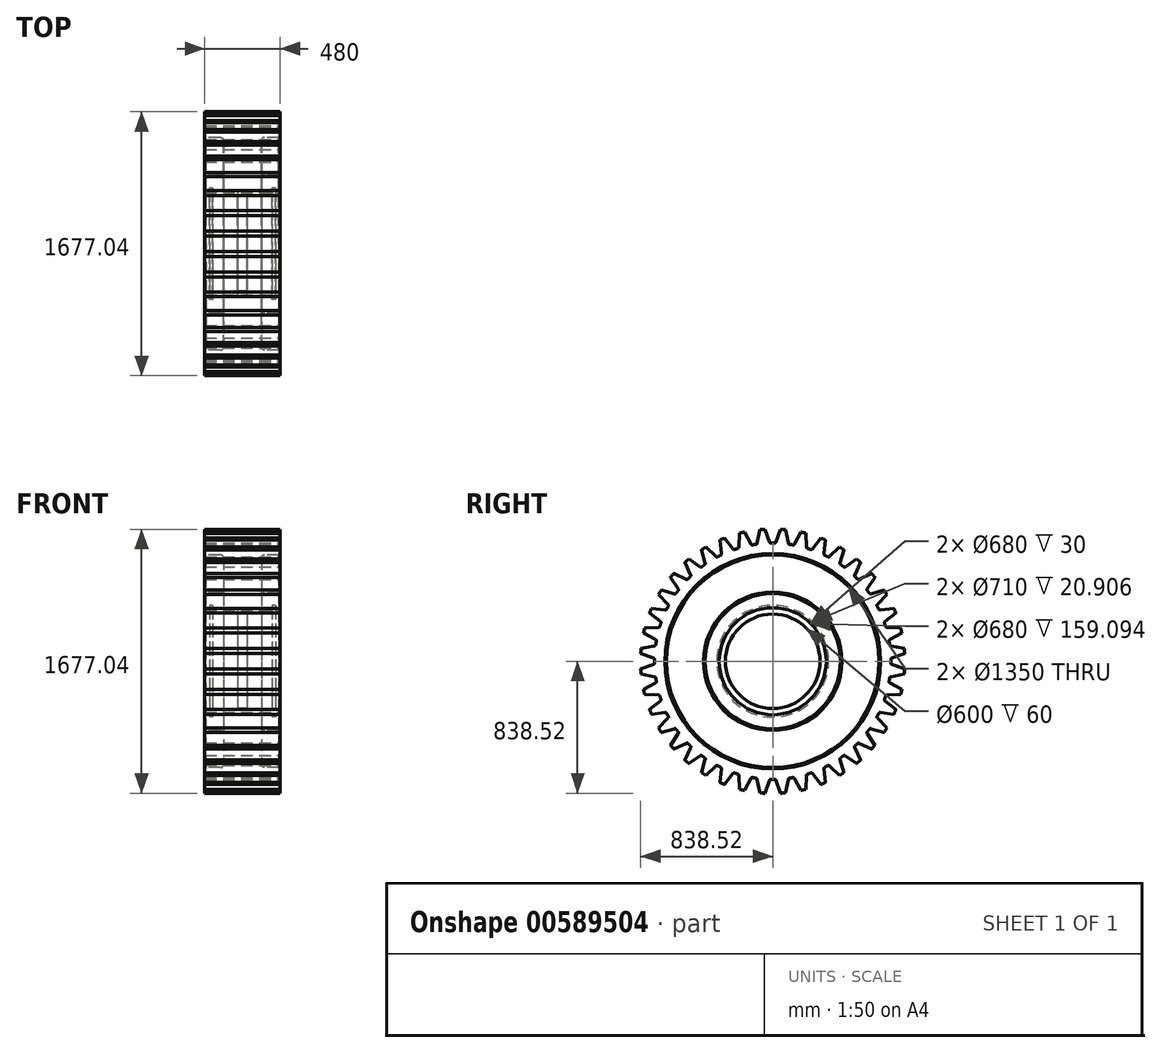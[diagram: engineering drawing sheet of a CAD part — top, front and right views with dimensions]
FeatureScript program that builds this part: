
annotation { "Feature Type Name" : "Feature", "Feature Type Description" : "" }
export const myFeature = defineFeature(function(context is Context, id is Id, definition is map)
    precondition{}
    {
        {
            var Q0;
            Q0=qCreatedBy(makeId("Front.planeOp"),FACE);
            var sketch = newSketch(context, id + "F0", { "sketchPlane" : qUnion([Q0])});
            skLineSegment(sketch, "E0", {"start": v(0, 0) * mm, "end": v(0, 840) * mm, "construction": true});
            skLineSegment(sketch, "E1", {"start": v(0, 840) * mm, "end": v(-240, 840) * mm});
            skLineSegment(sketch, "E2", {"start": v(-240, 840) * mm, "end": v(-240, 675) * mm});
            skLineSegment(sketch, "E3", {"start": v(-240, 0) * mm, "end": v(0, 0) * mm, "construction": true});
            skLineSegment(sketch, "E4", {"start": v(-240, 340) * mm, "end": v(-210, 340) * mm});
            skLineSegment(sketch, "E5", {"start": v(-210, 340) * mm, "end": v(-210, 355) * mm});
            skLineSegment(sketch, "E6", {"start": v(-210, 355) * mm, "end": v(-189.1, 355) * mm});
            skLineSegment(sketch, "E7", {"start": v(-189.1, 355) * mm, "end": v(-189.1, 340) * mm});
            skLineSegment(sketch, "E8", {"start": v(-189.1, 340) * mm, "end": v(-30, 340) * mm});
            skLineSegment(sketch, "E9", {"start": v(-30, 340) * mm, "end": v(-30, 300) * mm});
            skLineSegment(sketch, "E10", {"start": v(-30, 300) * mm, "end": v(0, 300) * mm});
            skLineSegment(sketch, "E11", {"start": v(-240, 440) * mm, "end": v(-140, 440) * mm});
            skLineSegment(sketch, "E12", {"start": v(-120, 460) * mm, "end": v(-120, 655) * mm});
            skLineSegment(sketch, "E13", {"start": v(-140, 675) * mm, "end": v(-240, 675) * mm});
            skLineSegment(sketch, "E14.trimOffspring", {"start": v(-240, 440) * mm, "end": v(-240, 340) * mm});
            skPoint(sketch, "E15.visualSharp", {"position": v(-120, 675) * mm});
            skArc(sketch, "E15.filletArc", {"start": v(-120, 655) * mm, "mid": v(-125.86, 669.14) * mm, "end": v(-140, 675) * mm});
            skPoint(sketch, "E16.visualSharp", {"position": v(-120, 440) * mm});
            skArc(sketch, "E16.filletArc", {"start": v(-140, 440) * mm, "mid": v(-125.86, 445.86) * mm, "end": v(-120, 460) * mm});
            skLineSegment(sketch, "E17.MirrorCS", {"start": v(0, 840) * mm, "end": v(240, 840) * mm});
            skLineSegment(sketch, "E18.MirrorCS", {"start": v(240, 840) * mm, "end": v(240, 675) * mm});
            skLineSegment(sketch, "E19.MirrorCS", {"start": v(140, 675) * mm, "end": v(240, 675) * mm});
            skArc(sketch, "E20.MirrorCS", {"start": v(120, 655) * mm, "mid": v(125.86, 669.14) * mm, "end": v(140, 675) * mm});
            skLineSegment(sketch, "E21.MirrorCS", {"start": v(120, 460) * mm, "end": v(120, 655) * mm});
            skArc(sketch, "E22.MirrorCS", {"start": v(140, 440) * mm, "mid": v(125.86, 445.86) * mm, "end": v(120, 460) * mm});
            skLineSegment(sketch, "E23.MirrorCS", {"start": v(240, 440) * mm, "end": v(140, 440) * mm});
            skLineSegment(sketch, "E24.MirrorCS", {"start": v(240, 440) * mm, "end": v(240, 340) * mm});
            skLineSegment(sketch, "E25.MirrorCS", {"start": v(240, 340) * mm, "end": v(210, 340) * mm});
            skLineSegment(sketch, "E26.MirrorCS", {"start": v(210, 340) * mm, "end": v(210, 355) * mm});
            skLineSegment(sketch, "E27.MirrorCS", {"start": v(210, 355) * mm, "end": v(189.1, 355) * mm});
            skLineSegment(sketch, "E28.MirrorCS", {"start": v(189.1, 355) * mm, "end": v(189.1, 340) * mm});
            skLineSegment(sketch, "E29.MirrorCS", {"start": v(189.1, 340) * mm, "end": v(30, 340) * mm});
            skLineSegment(sketch, "E30.MirrorCS", {"start": v(30, 340) * mm, "end": v(30, 300) * mm});
            skLineSegment(sketch, "E31.MirrorCS", {"start": v(30, 300) * mm, "end": v(0, 300) * mm});
            skSolve(sketch);
        }
        {
            var Q0;
            Q0=makeQuery(id+"F0.imprint","IMPRINT",FACE,{"disambiguationData":[TD([[makeQuery(id+"F0.imprint","IMPRINT",EDGE,{"derivedFrom":sQuery(id+"F0.wireOp",EDGE,"E1")}),1.0]])]});
            var Q1;
            Q1=sQuery(id+"F0.wireOp",EDGE,"E3");
            revolve(context, id + "F1", {"entities" : qUnion([Q0]), "axis" : qUnion([Q1]), "revolveType" : RevolveType.FULL});
        }
        {
            var Q0;
            Q0=qCreatedBy(makeId("Right.planeOp"),FACE);
            var sketch = newSketch(context, id + "F2", { "sketchPlane" : qUnion([Q0])});
            skArc(sketch, "E32.0", {"start": v(10.41, 749.93) * mm, "mid": v(0, 750) * mm, "end": v(-10.41, 749.93) * mm});
            skLineSegment(sketch, "E33", {"start": v(0, 0) * mm, "end": v(0, 841.09) * mm, "construction": true});
            skLineSegment(sketch, "E34", {"start": v(19.95, 756.5) * mm, "end": v(49.8, 838.52) * mm});
            skLineSegment(sketch, "E35.MirrorCS", {"start": v(-19.95, 756.5) * mm, "end": v(-49.8, 838.52) * mm});
            skPoint(sketch, "E36.visualSharp", {"position": v(-17.5, 749.8) * mm});
            skArc(sketch, "E36.filletArc", {"start": v(-19.95, 756.5) * mm, "mid": v(-16.23, 751.7) * mm, "end": v(-10.41, 749.93) * mm});
            skPoint(sketch, "E37.visualSharp", {"position": v(17.5, 749.8) * mm});
            skArc(sketch, "E37.filletArc", {"start": v(10.41, 749.93) * mm, "mid": v(16.23, 751.7) * mm, "end": v(19.95, 756.5) * mm});
            skArc(sketch, "E38", {"start": v(49.8, 838.52) * mm, "mid": v(0, 840) * mm, "end": v(-49.8, 838.52) * mm});
            skSolve(sketch);
        }
        {
            var Q0;
            Q0 = qSketchRegion(id + "F2", true);
            extrude(context, id + "F3", {"entities" : qUnion([Q0]), "operationType" : NewBodyOperationType.REMOVE, "endBound" : BoundingType.SYMMETRIC, "oppositeDirection" : true, "depth" : 500 * mm, "offsetDistance" : 25 * mm});
        }
        {
            var Q0;
            Q0=makeQuery(id+"F3.boolean.opBoolean","COPY",FACE,{"derivedFrom":makeQuery(id+"F3.opExtrude","SWEPT_FACE",FACE,{"disambiguationData":[OSD([sQuery(id+"F2.wireOp",EDGE,"E35.MirrorCS")])]})});
            var Q1;
            Q1=makeQuery(id+"F3.boolean.opBoolean","COPY",FACE,{"derivedFrom":makeQuery(id+"F3.opExtrude","SWEPT_FACE",FACE,{"disambiguationData":[OSD([sQuery(id+"F2.wireOp",EDGE,"E36.filletArc")])]})});
            var Q2;
            Q2=makeQuery(id+"F3.boolean.opBoolean","COPY",FACE,{"derivedFrom":makeQuery(id+"F3.opExtrude","SWEPT_FACE",FACE,{"disambiguationData":[OSD([sQuery(id+"F2.wireOp",EDGE,"E32.0")])]})});
            var Q3;
            Q3=makeQuery(id+"F3.boolean.opBoolean","COPY",FACE,{"derivedFrom":makeQuery(id+"F3.opExtrude","SWEPT_FACE",FACE,{"disambiguationData":[OSD([sQuery(id+"F2.wireOp",EDGE,"E37.filletArc")])]})});
            var Q4;
            Q4=makeQuery(id+"F3.boolean.opBoolean","COPY",FACE,{"derivedFrom":makeQuery(id+"F3.opExtrude","SWEPT_FACE",FACE,{"disambiguationData":[OSD([sQuery(id+"F2.wireOp",EDGE,"E34")])]})});
            var Q5;
            Q5=makeQuery(id+"F1.opRevolve","SWEPT_FACE",FACE,{"disambiguationData":[OSD([sQuery(id+"F0.wireOp",EDGE,"E1"),sQuery(id+"F0.wireOp",EDGE,"E17.MirrorCS")])]});
            circularPattern(context, id + "F4", {"patternType" : PatternType.FACE, "faces" : qUnion([Q0, Q1, Q2, Q3, Q4]), "axis" : qUnion([Q5]), "angle" : 9 * degree, "instanceCount" : 40});
        }
        {
            var Q0;
            Q0=makeQuery(id+"F1.opRevolve","SWEPT_EDGE",EDGE,{"disambiguationData":[OSD([sQuery(id+"F0.wireOp",EDGE,"E18.MirrorCS"),sQuery(id+"F0.wireOp",EDGE,"E19.MirrorCS")])]});
            var Q1;
            Q1=makeQuery(id+"F1.opRevolve","SWEPT_EDGE",EDGE,{"disambiguationData":[OSD([sQuery(id+"F0.wireOp",EDGE,"E23.MirrorCS"),sQuery(id+"F0.wireOp",EDGE,"E24.MirrorCS")])]});
            var Q2;
            Q2=makeQuery(id+"F1.opRevolve","SWEPT_EDGE",EDGE,{"disambiguationData":[OSD([sQuery(id+"F0.wireOp",EDGE,"E2"),sQuery(id+"F0.wireOp",EDGE,"E13")])]});
            var Q3;
            Q3=makeQuery(id+"F1.opRevolve","SWEPT_EDGE",EDGE,{"disambiguationData":[OSD([sQuery(id+"F0.wireOp",EDGE,"E11"),sQuery(id+"F0.wireOp",EDGE,"E14.trimOffspring")])]});
            chamfer(context, id + "F5", {"entities" : qUnion([Q0, Q1, Q2, Q3]), "width" : 10 * mm, "tangentPropagation" : true});
        }
    });
